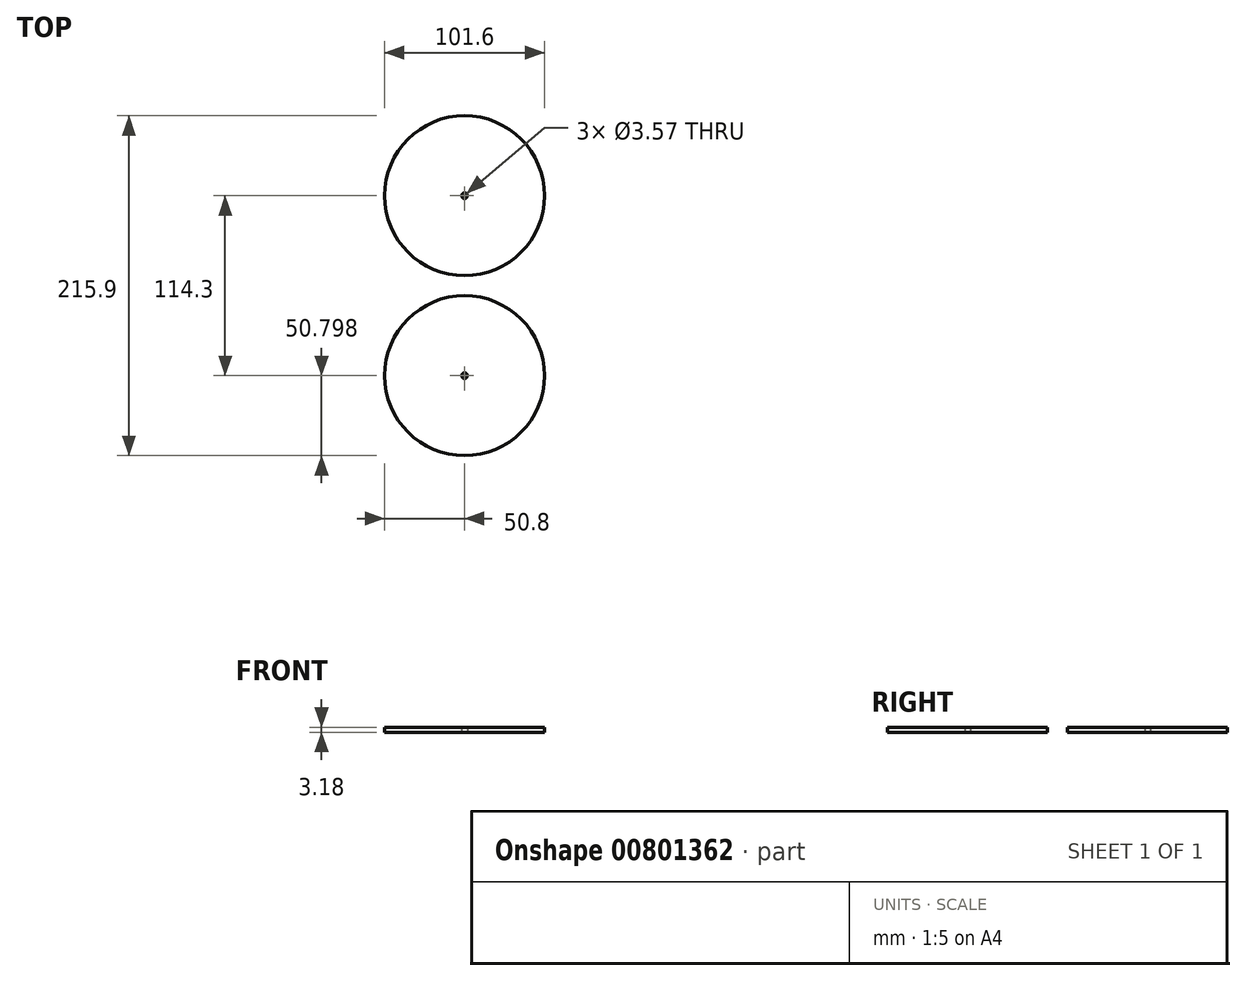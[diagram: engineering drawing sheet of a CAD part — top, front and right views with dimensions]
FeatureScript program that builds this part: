
annotation { "Feature Type Name" : "Feature", "Feature Type Description" : "" }
export const myFeature = defineFeature(function(context is Context, id is Id, definition is map)
    precondition{}
    {
        {
            var Q0;
            Q0=qCreatedBy(makeId("Top.planeOp"),FACE);
            var sketch = newSketch(context, id + "F0", { "sketchPlane" : qUnion([Q0])});
            skCircle(sketch, "E0", {"center": v(0, -48.55) * mm, "radius": 50.8 * mm});
            skCircle(sketch, "E1", {"center": v(0, -162.85) * mm, "radius": 50.8 * mm});
            skCircle(sketch, "E2", {"center": v(0, -48.55) * mm, "radius": 1.79 * mm});
            skCircle(sketch, "E3", {"center": v(0, -162.85) * mm, "radius": 1.79 * mm});
            skSolve(sketch);
        }
        {
            var Q0;
            Q0=makeQuery(id+"F0.imprint","IMPRINT",FACE,{"disambiguationData":[TD([[makeQuery(id+"F0.imprint","IMPRINT",EDGE,{"derivedFrom":sQuery(id+"F0.wireOp",EDGE,"E0")}),1.0]])]});
            extrude(context, id + "F1", {"entities" : qUnion([Q0]), "depth" : 3.17 * mm, "offsetDistance" : 25.4 * mm});
        }
        {
            var Q0;
            Q0 = qSketchRegion(id + "F0", true);
            extrude(context, id + "F2", {"entities" : qUnion([Q0]), "depth" : 3.17 * mm, "offsetDistance" : 25.4 * mm});
        }
    });
